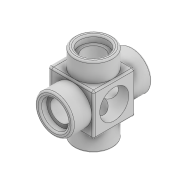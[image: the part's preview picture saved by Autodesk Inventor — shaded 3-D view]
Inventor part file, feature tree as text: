
AUTODESK INVENTOR PART (.ipt)
format: ipt  version: 2020 (Build 240168000, 168)  size: 563,200 bytes
history: native  units: mm
features: extrude x11, sketch x11, fillet x3, mirror x2, plane x1, projected_geometry x1
ambient origin geometry x8: Origin, YZ Plane, XZ Plane, XY Plane, X Axis, Y Axis, Z Axis, Center Point
bodies: Solid1 (feature_tree)
feature tree (29):
  extrude  "Extrusion1"  Depth=6.0mm
  extrude  "Extrusion2"  Depth=5.5mm
  extrude  "Extrusion3"  Depth=5.5mm
  extrude  "Extrusion4"  Depth=5.5mm
  extrude  "Extrusion5"  Depth=5.5mm
  extrude  "Extrusion7"  Depth=3.0mm
  extrude  "Extrusion8"  Depth=3.0mm
  extrude  "Extrusion9"  Depth=4.0mm
  extrude  "Extrusion10"  Depth=4.0mm
  mirror  "Mirror1"
  mirror  "Mirror2"
  extrude  "Extrusion11"  Depth=1.0mm TaperAngle=0.0deg
  extrude  "Extrusion12"  Depth=5.5mm TaperAngle=0.0deg
  fillet  "Fillet4"  Radius=0.25mm
  fillet  "Fillet5"  Radius=0.25mm
  fillet  "Fillet6"  Radius=1.0mm
  sketch  "Sketch1"  dims[d0=6.0mm d1=6.0mm]
  sketch  "Sketch2"  dims[d2=6.0mm d3=0.0mm d4=5.5mm]
  sketch  "Sketch3"  dims[d5=2.75mm d6=0.0mm d7=5.5mm]
  sketch  "Sketch4"  dims[d8=2.75mm d9=0.0mm d10=5.5mm]
  sketch  "Sketch5"  dims[d11=2.75mm d12=0.0mm d13=5.5mm]
  sketch  "Sketch8"  dims[d14=2.75mm d15=0.0mm d23=3.0mm]
  sketch  "Sketch9"  dims[d24=0.0mm d25=0.0mm d26=3.0mm]
  sketch  "Sketch10"  dims[d27=0.0mm d28=0.0mm d30=4.0mm]
  sketch  "Sketch11"  dims[d31=1.0mm d32=0.0mm d33=4.0mm]
  plane  "Work Plane1"
  sketch  "Sketch12"  dims[d34=1.0mm d35=0.0mm d36=1.0mm d37=0.0mm]
  projected_geometry  "Projected Loop1"
  sketch  "Sketch13"  dims[d38=4.2mm d39=5.5mm d40=0.0mm d41=0.25mm d42=0.25mm d43=1.0mm]
